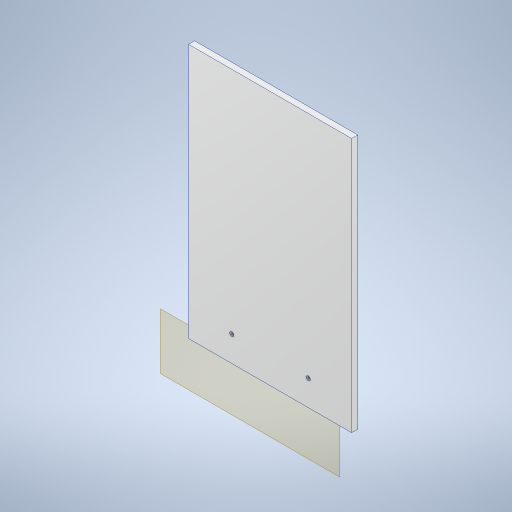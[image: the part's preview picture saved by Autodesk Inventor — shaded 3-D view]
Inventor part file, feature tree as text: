
AUTODESK INVENTOR PART (.ipt)
format: ipt  version: 2023.2 (Build 272271000, 271)  size: 240,128 bytes
history: native  units: mm
features: reference x3, other x3, plane x1, extrude x1, sketch x1
ambient origin geometry x8: Origin, YZ Plane, XZ Plane, XY Plane, X Axis, Y Axis, Z Axis, Center Point
bodies: Solid1 (feature_tree)
feature tree (9):
  plane  "Work Plane1"
  extrude  "Extrusion1"  Depth=6.0mm TaperAngle=0.0deg
  sketch  "Sketch1"  dims[d0=200.0mm d1=6.0mm d2=0.0mm]
  reference  "Reference1"
  reference  "Reference2"
  reference  "Reference3"
  parser-record x1  (decoder bookkeeping rows leaked as tree rows — omitted from the tree; the rows remain in map.json)
  other  "Main Assembly.iam"
  other  "Joining Brace Front:1"
note: 1 file-system path scrubbed to <path> (originals preserved in map.json)
